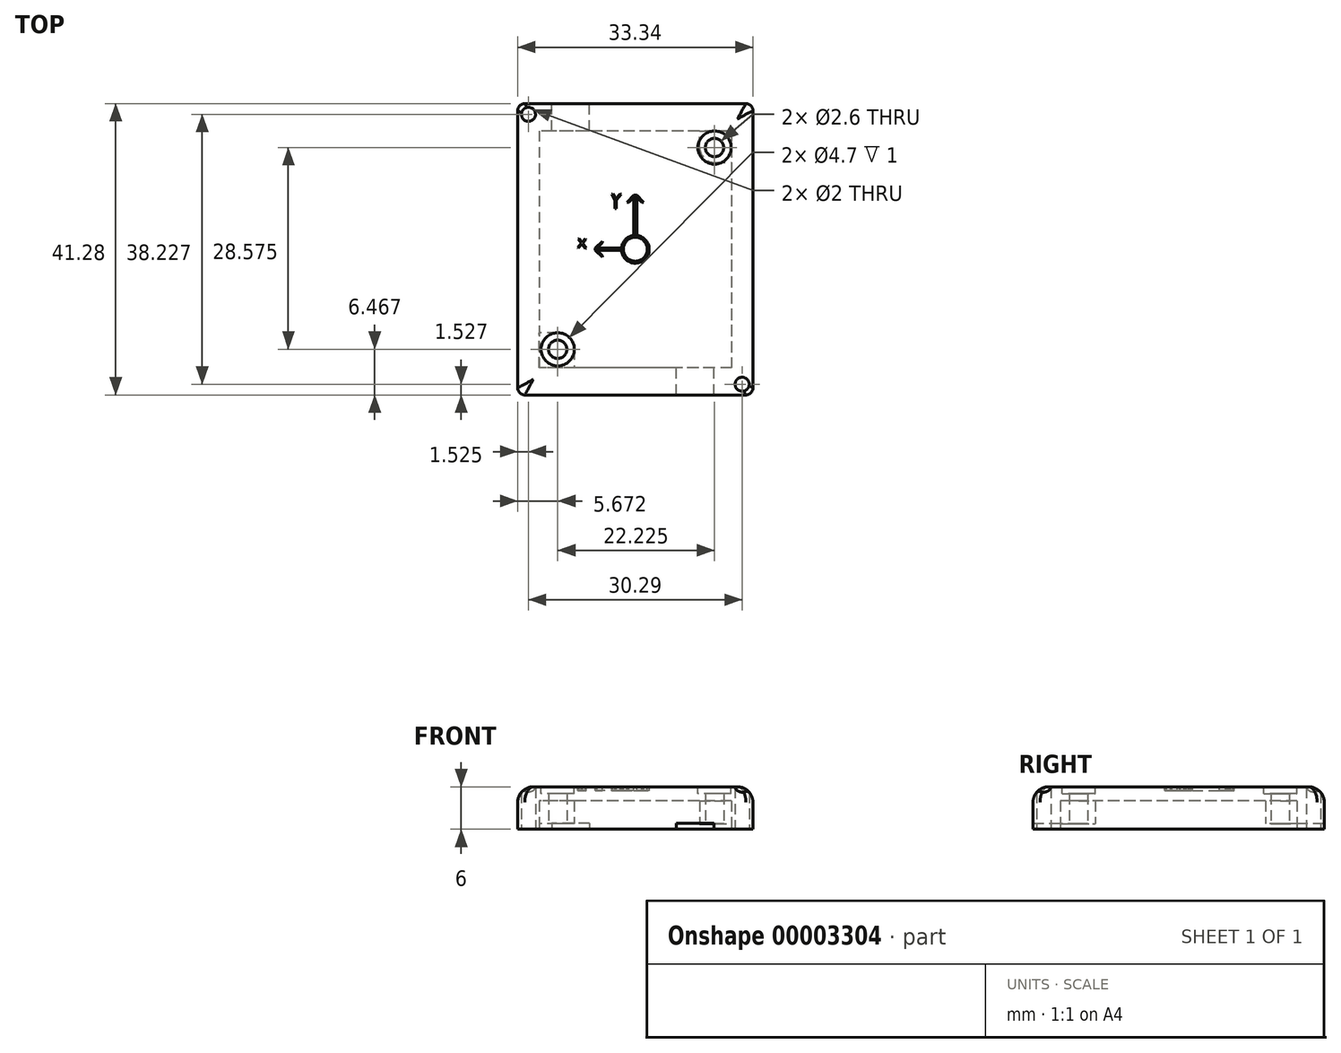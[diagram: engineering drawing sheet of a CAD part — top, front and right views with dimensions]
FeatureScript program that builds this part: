
annotation { "Feature Type Name" : "Feature", "Feature Type Description" : "" }
export const myFeature = defineFeature(function(context is Context, id is Id, definition is map)
    precondition{}
    {
        {
            var Q0;
            Q0=qCreatedBy(makeId("Top.planeOp"),FACE);
            var sketch = newSketch(context, id + "F0", { "sketchPlane" : qUnion([Q0])});
            skLineSegment(sketch, "E0.rect.bottom", {"start": v(16.67, 20.64) * mm, "end": v(-16.67, 20.64) * mm});
            skLineSegment(sketch, "E0.rect.top", {"start": v(16.67, -20.64) * mm, "end": v(-16.67, -20.64) * mm});
            skLineSegment(sketch, "E0.rect.left", {"start": v(16.67, 20.64) * mm, "end": v(16.67, -20.64) * mm});
            skLineSegment(sketch, "E0.rect.right", {"start": v(-16.67, 20.64) * mm, "end": v(-16.67, -20.64) * mm});
            skPoint(sketch, "E0.rect.middle", {"position": v(0, 0) * mm});
            skSolve(sketch);
        }
        {
            var Q0;
            Q0=qSketchRegion(id+"F0",true);
            extrude(context, id + "F1", {"entities" : qUnion([Q0]), "oppositeDirection" : true, "depth" : 6 * mm});
        }
        {
            var Q0;
            Q0=makeQuery(id+"F1.opExtrude","CAP_FACE",FACE,{"disambiguationData":[OSD([sQuery(id+"F0.wireOp",EDGE,"E0.rect.bottom"),sQuery(id+"F0.wireOp",EDGE,"E0.rect.top"),sQuery(id+"F0.wireOp",EDGE,"E0.rect.left"),sQuery(id+"F0.wireOp",EDGE,"E0.rect.right")])],"isStart":true});
            var sketch = newSketch(context, id + "F2", { "sketchPlane" : qUnion([Q0])});
            skLineSegment(sketch, "E1.rect.bottom", {"start": v(13.33, 16.51) * mm, "end": v(-13.34, 16.51) * mm});
            skLineSegment(sketch, "E1.rect.top", {"start": v(13.34, -16.51) * mm, "end": v(-13.33, -16.51) * mm});
            skLineSegment(sketch, "E1.rect.left", {"start": v(13.33, 16.51) * mm, "end": v(13.34, -16.51) * mm});
            skLineSegment(sketch, "E1.rect.right", {"start": v(-13.34, 16.51) * mm, "end": v(-13.33, -16.51) * mm});
            skPoint(sketch, "E1.rect.middle", {"position": v(0, 0) * mm});
            skCircle(sketch, "E2", {"center": v(11.23, 14.4) * mm, "radius": 1.25 * mm});
            skCircle(sketch, "E3", {"center": v(-11, -14.17) * mm, "radius": 1.25 * mm});
            skCircle(sketch, "E4", {"center": v(11.23, 14.4) * mm, "radius": 2.1 * mm});
            skCircle(sketch, "E5", {"center": v(-11, -14.17) * mm, "radius": 2.34 * mm});
            skLineSegment(sketch, "E6.0", {"start": v(13.59, 16.76) * mm, "end": v(-13.59, 16.76) * mm});
            skLineSegment(sketch, "E6.1", {"start": v(13.59, 16.76) * mm, "end": v(13.59, -16.76) * mm});
            skLineSegment(sketch, "E6.2", {"start": v(13.59, -16.76) * mm, "end": v(-13.59, -16.76) * mm});
            skLineSegment(sketch, "E6.3", {"start": v(-13.59, 16.76) * mm, "end": v(-13.59, -16.76) * mm});
            skLineSegment(sketch, "E7", {"start": v(9.12, 14.4) * mm, "end": v(9.12, 16.76) * mm});
            skLineSegment(sketch, "E8", {"start": v(11.23, 12.3) * mm, "end": v(13.59, 12.3) * mm});
            skLineSegment(sketch, "E9", {"start": v(-11, -11.84) * mm, "end": v(-13.59, -11.84) * mm});
            skLineSegment(sketch, "E10", {"start": v(-8.66, -14.17) * mm, "end": v(-8.66, -16.76) * mm});
            skSolve(sketch);
        }
        {
            var Q0;
            {var subQ6=sQuery(id+"F2.wireOp",EDGE,"E1.rect.right");var subQ10=sQuery(id+"F2.wireOp",EDGE,"E1.rect.bottom");var subQ18=makeQuery(id+"F2.imprint","INTERSECT",VERTEX,{"derivedFrom":[subQ10,subQ6]});Q0=makeQuery(id+"F2.imprint","IMPRINT",FACE,{"disambiguationData":[TD([[makeQuery(id+"F2.imprint","IMPRINT",EDGE,{"disambiguationData":[TD([[subQ18,1.0]])],"derivedFrom":subQ10}),1.0]])]});}
            var Q1;
            {var subQ1=sQuery(id+"F2.wireOp",EDGE,"E1.rect.right");var subQ6=sQuery(id+"F2.wireOp",EDGE,"E1.rect.bottom");var subQ11=makeQuery(id+"F2.imprint","INTERSECT",VERTEX,{"derivedFrom":[subQ6,subQ1]});Q1=makeQuery(id+"F2.imprint","IMPRINT",FACE,{"disambiguationData":[TD([[makeQuery(id+"F2.imprint","IMPRINT",EDGE,{"disambiguationData":[TD([[subQ11,1.0]])],"derivedFrom":subQ6}),-1.0]])]});}
            var Q2;
            {var subQ1=sQuery(id+"F2.wireOp",EDGE,"E1.rect.left");var subQ6=sQuery(id+"F2.wireOp",EDGE,"E1.rect.top");var subQ11=makeQuery(id+"F2.imprint","INTERSECT",VERTEX,{"derivedFrom":[subQ6,subQ1]});Q2=makeQuery(id+"F2.imprint","IMPRINT",FACE,{"disambiguationData":[TD([[makeQuery(id+"F2.imprint","IMPRINT",EDGE,{"disambiguationData":[TD([[subQ11,-1.0]])],"derivedFrom":subQ6}),1.0]])]});}
            extrude(context, id + "F3", {"entities" : qUnion([Q0, Q1, Q2]), "operationType" : NewBodyOperationType.REMOVE, "oppositeDirection" : true, "depth" : 4 * mm});
        }
        {
            var Q0;
            Q0=makeQuery(id+"F1.opExtrude","CAP_FACE",FACE,{"disambiguationData":[OSD([sQuery(id+"F0.wireOp",EDGE,"E0.rect.bottom"),sQuery(id+"F0.wireOp",EDGE,"E0.rect.top"),sQuery(id+"F0.wireOp",EDGE,"E0.rect.left"),sQuery(id+"F0.wireOp",EDGE,"E0.rect.right")])],"isStart":true});
            var sketch = newSketch(context, id + "F4", { "sketchPlane" : qUnion([Q0])});
            skLineSegment(sketch, "E11", {"start": v(9.12, 16.76) * mm, "end": v(13.59, 16.76) * mm});
            skLineSegment(sketch, "E12", {"start": v(13.59, 16.76) * mm, "end": v(13.59, 12.3) * mm});
            skLineSegment(sketch, "E13", {"start": v(13.59, 12.3) * mm, "end": v(11.23, 12.3) * mm});
            skArc(sketch, "E14", {"start": v(9.12, 14.4) * mm, "mid": v(9.74, 12.91) * mm, "end": v(11.23, 12.3) * mm});
            skLineSegment(sketch, "E15", {"start": v(9.12, 14.4) * mm, "end": v(9.12, 16.76) * mm});
            skArc(sketch, "E16", {"start": v(-8.66, -14.17) * mm, "mid": v(-9.35, -12.52) * mm, "end": v(-11, -11.84) * mm});
            skLineSegment(sketch, "E17", {"start": v(-8.66, -14.17) * mm, "end": v(-8.66, -16.76) * mm});
            skLineSegment(sketch, "E18", {"start": v(-8.66, -16.76) * mm, "end": v(-13.59, -16.76) * mm});
            skLineSegment(sketch, "E19", {"start": v(-13.59, -16.76) * mm, "end": v(-13.59, -11.84) * mm});
            skLineSegment(sketch, "E20", {"start": v(-13.59, -11.84) * mm, "end": v(-11, -11.84) * mm});
            skSolve(sketch);
        }
        {
            var Q0;
            Q0=qSketchRegion(id+"F4",true);
            extrude(context, id + "F5", {"entities" : qUnion([Q0]), "operationType" : NewBodyOperationType.REMOVE, "oppositeDirection" : true, "depth" : .8 * mm});
        }
        {
            var Q0;
            Q0=makeQuery(id+"F5.boolean.opBoolean","COPY",FACE,{"derivedFrom":makeQuery(id+"F5.opExtrude","CAP_FACE",FACE,{"disambiguationData":[OSD([sQuery(id+"F4.wireOp",EDGE,"E11"),sQuery(id+"F4.wireOp",EDGE,"E12"),sQuery(id+"F4.wireOp",EDGE,"E13"),sQuery(id+"F4.wireOp",EDGE,"E14"),sQuery(id+"F4.wireOp",EDGE,"E15")])],"isStart":false})});
            var sketch = newSketch(context, id + "F6", { "sketchPlane" : qUnion([Q0])});
            skCircle(sketch, "E21", {"center": v(11.23, 14.4) * mm, "radius": 1.3 * mm});
            skSolve(sketch);
        }
        {
            var Q0;
            Q0=qSketchRegion(id+"F6",true);
            extrude(context, id + "F7", {"entities" : qUnion([Q0]), "operationType" : NewBodyOperationType.REMOVE, "oppositeDirection" : true, "depth" : 25.4 * mm});
        }
        {
            var Q0;
            Q0=makeQuery(id+"F5.boolean.opBoolean","COPY",FACE,{"derivedFrom":makeQuery(id+"F5.opExtrude","CAP_FACE",FACE,{"disambiguationData":[OSD([sQuery(id+"F4.wireOp",EDGE,"E16"),sQuery(id+"F4.wireOp",EDGE,"E17"),sQuery(id+"F4.wireOp",EDGE,"E18"),sQuery(id+"F4.wireOp",EDGE,"E19"),sQuery(id+"F4.wireOp",EDGE,"E20")])],"isStart":false})});
            var sketch = newSketch(context, id + "F8", { "sketchPlane" : qUnion([Q0])});
            skCircle(sketch, "E22", {"center": v(-11, -14.17) * mm, "radius": 1.3 * mm});
            skSolve(sketch);
        }
        {
            var Q0;
            Q0=qSketchRegion(id+"F8",true);
            extrude(context, id + "F9", {"entities" : qUnion([Q0]), "operationType" : NewBodyOperationType.REMOVE, "oppositeDirection" : true, "depth" : 25.4 * mm});
        }
        {
            var Q0;
            Q0=makeQuery(id+"F1.opExtrude","CAP_FACE",FACE,{"disambiguationData":[OSD([sQuery(id+"F0.wireOp",EDGE,"E0.rect.bottom"),sQuery(id+"F0.wireOp",EDGE,"E0.rect.top"),sQuery(id+"F0.wireOp",EDGE,"E0.rect.left"),sQuery(id+"F0.wireOp",EDGE,"E0.rect.right")])],"isStart":true});
            var sketch = newSketch(context, id + "F10", { "sketchPlane" : qUnion([Q0])});
            skLineSegment(sketch, "E23.bottom", {"start": v(-13.59, 16.76) * mm, "end": v(-5.09, 16.76) * mm});
            skLineSegment(sketch, "E23.top", {"start": v(-13.59, 20.64) * mm, "end": v(-5.09, 20.64) * mm});
            skLineSegment(sketch, "E23.left", {"start": v(-13.59, 16.76) * mm, "end": v(-13.59, 20.64) * mm});
            skLineSegment(sketch, "E23.right", {"start": v(-5.09, 16.76) * mm, "end": v(-5.09, 20.64) * mm});
            skLineSegment(sketch, "E24.bottom", {"start": v(13.59, -16.76) * mm, "end": v(4.59, -16.76) * mm});
            skLineSegment(sketch, "E24.top", {"start": v(13.59, -20.64) * mm, "end": v(4.59, -20.64) * mm});
            skLineSegment(sketch, "E24.left", {"start": v(13.59, -16.76) * mm, "end": v(13.59, -20.64) * mm});
            skLineSegment(sketch, "E24.right", {"start": v(4.59, -16.76) * mm, "end": v(4.59, -20.64) * mm});
            skSolve(sketch);
        }
        {
            var Q0;
            Q0=qSketchRegion(id+"F10",true);
            extrude(context, id + "F11", {"entities" : qUnion([Q0]), "operationType" : NewBodyOperationType.REMOVE, "oppositeDirection" : true, "depth" : .4 * mm});
        }
        {
            var Q0;
            Q0=makeQuery(id+"F1.opExtrude","SWEPT_BODY",BODY,{"disambiguationData":[OSD([sQuery(id+"F0.wireOp",EDGE,"E0.rect.bottom"),sQuery(id+"F0.wireOp",EDGE,"E0.rect.top"),sQuery(id+"F0.wireOp",EDGE,"E0.rect.left"),sQuery(id+"F0.wireOp",EDGE,"E0.rect.right")])]});
            var Q1;
            Q1=qCreatedBy(makeId("Top.planeOp"),FACE);
            mirror(context, id + "F12", {"entities" : qUnion([Q0]), "mirrorPlane" : qUnion([Q1])});
        }
        {
            var Q0;
            Q0=makeQuery(id+"F1.opExtrude","SWEPT_BODY",BODY,{"disambiguationData":[OSD([sQuery(id+"F0.wireOp",EDGE,"E0.rect.bottom"),sQuery(id+"F0.wireOp",EDGE,"E0.rect.top"),sQuery(id+"F0.wireOp",EDGE,"E0.rect.left"),sQuery(id+"F0.wireOp",EDGE,"E0.rect.right")])]});
            deleteBodies(context, id + "F13", {"entities" : qUnion([Q0])});
        }
        {
            var Q0;
            Q0=makeQuery(id+"F12.opPattern","COPY",FACE,{"derivedFrom":makeQuery(id+"F1.opExtrude","CAP_FACE",FACE,{"disambiguationData":[OSD([sQuery(id+"F0.wireOp",EDGE,"E0.rect.bottom"),sQuery(id+"F0.wireOp",EDGE,"E0.rect.top"),sQuery(id+"F0.wireOp",EDGE,"E0.rect.left"),sQuery(id+"F0.wireOp",EDGE,"E0.rect.right")])],"isStart":false}),"instanceName":"1"});
            var sketch = newSketch(context, id + "F14", { "sketchPlane" : qUnion([Q0])});
            skCircle(sketch, "E25", {"center": v(11.23, 14.4) * mm, "radius": 2.35 * mm});
            skCircle(sketch, "E26", {"center": v(-11, -14.17) * mm, "radius": 2.35 * mm});
            skSolve(sketch);
        }
        {
            var Q0;
            Q0 = qSketchRegion(id + "F14", true);
            extrude(context, id + "F15", {"entities" : qUnion([Q0]), "operationType" : NewBodyOperationType.REMOVE, "oppositeDirection" : true, "depth" : 1 * mm});
        }
        {
            var Q0;
            {var subQ0=sQuery(id+"F0.wireOp",EDGE,"E0.rect.bottom");var subQ1=sQuery(id+"F0.wireOp",EDGE,"E0.rect.top");var subQ2=sQuery(id+"F0.wireOp",EDGE,"E0.rect.right");Q0=makeQuery(id+"F12.opPattern","COPY",FACE,{"derivedFrom":makeQuery(id+"F11.boolean.opBoolean","SPLIT",FACE,{"disambiguationData":[TD([makeQuery(id+"F1.opExtrude","SWEPT_FACE",FACE,{"disambiguationData":[OSD([subQ2])]})])],"derivedFrom":makeQuery(id+"F1.opExtrude","CAP_FACE",FACE,{"disambiguationData":[OSD([subQ0,subQ1,sQuery(id+"F0.wireOp",EDGE,"E0.rect.left"),subQ2])],"isStart":true})}),"instanceName":"1"});}
            var sketch = newSketch(context, id + "F16", { "sketchPlane" : qUnion([Q0])});
            skCircle(sketch, "E27", {"center": v(-15.14, -19.11) * mm, "radius": 1 * mm});
            skSolve(sketch);
        }
        {
            var Q0;
            Q0=makeQuery(id+"F16.imprint","IMPRINT",FACE,{"disambiguationData":[TD([[makeQuery(id+"F16.imprint","IMPRINT",EDGE,{"derivedFrom":sQuery(id+"F16.wireOp",EDGE,"E27")}),1.0]])]});
            extrude(context, id + "F17", {"entities" : qUnion([Q0]), "operationType" : NewBodyOperationType.REMOVE, "oppositeDirection" : true, "depth" : 20 * mm});
        }
        {
            var Q0;
            {var subQ0=sQuery(id+"F0.wireOp",EDGE,"E0.rect.bottom");var subQ1=sQuery(id+"F0.wireOp",EDGE,"E0.rect.top");var subQ2=sQuery(id+"F0.wireOp",EDGE,"E0.rect.left");Q0=makeQuery(id+"F12.opPattern","COPY",FACE,{"derivedFrom":makeQuery(id+"F11.boolean.opBoolean","SPLIT",FACE,{"disambiguationData":[TD([makeQuery(id+"F1.opExtrude","SWEPT_FACE",FACE,{"disambiguationData":[OSD([subQ2])]})])],"derivedFrom":makeQuery(id+"F1.opExtrude","CAP_FACE",FACE,{"disambiguationData":[OSD([subQ0,subQ1,subQ2,sQuery(id+"F0.wireOp",EDGE,"E0.rect.right")])],"isStart":true})}),"instanceName":"1"});}
            var sketch = newSketch(context, id + "F18", { "sketchPlane" : qUnion([Q0])});
            skCircle(sketch, "E28", {"center": v(15.14, 19.11) * mm, "radius": 1 * mm});
            skSolve(sketch);
        }
        {
            var Q0;
            Q0 = qSketchRegion(id + "F18", true);
            extrude(context, id + "F19", {"entities" : qUnion([Q0]), "operationType" : NewBodyOperationType.REMOVE, "oppositeDirection" : true, "depth" : 25 * mm});
        }
        {
            var Q0;
            Q0=makeQuery(id+"F12.opPattern","COPY",EDGE,{"derivedFrom":makeQuery(id+"F1.opExtrude","CAP_EDGE",EDGE,{"disambiguationData":[OSD([sQuery(id+"F0.wireOp",EDGE,"E0.rect.top")])],"isStart":false}),"instanceName":"1"});
            var Q1;
            Q1=makeQuery(id+"F12.opPattern","COPY",EDGE,{"derivedFrom":makeQuery(id+"F1.opExtrude","CAP_EDGE",EDGE,{"disambiguationData":[OSD([sQuery(id+"F0.wireOp",EDGE,"E0.rect.left")])],"isStart":false}),"instanceName":"1"});
            var Q2;
            Q2=makeQuery(id+"F12.opPattern","COPY",EDGE,{"derivedFrom":makeQuery(id+"F1.opExtrude","CAP_EDGE",EDGE,{"disambiguationData":[OSD([sQuery(id+"F0.wireOp",EDGE,"E0.rect.bottom")])],"isStart":false}),"instanceName":"1"});
            var Q3;
            Q3=makeQuery(id+"F12.opPattern","COPY",EDGE,{"derivedFrom":makeQuery(id+"F1.opExtrude","CAP_EDGE",EDGE,{"disambiguationData":[OSD([sQuery(id+"F0.wireOp",EDGE,"E0.rect.right")])],"isStart":false}),"instanceName":"1"});
            fillet(context, id + "F20", {"entities" : qUnion([Q0, Q1, Q2, Q3]), "radius" : 2.2 * mm, "tangentPropagation" : true, "allowEdgeOverflow" : false});
        }
        {
            var Q0;
            Q0=makeQuery(id+"F12.opPattern","COPY",EDGE,{"derivedFrom":makeQuery(id+"F1.opExtrude","SWEPT_EDGE",EDGE,{"disambiguationData":[OSD([sQuery(id+"F0.wireOp",EDGE,"E0.rect.bottom"),sQuery(id+"F0.wireOp",EDGE,"E0.rect.right")])]}),"instanceName":"1"});
            var Q1;
            Q1=makeQuery(id+"F12.opPattern","COPY",EDGE,{"derivedFrom":makeQuery(id+"F1.opExtrude","SWEPT_EDGE",EDGE,{"disambiguationData":[OSD([sQuery(id+"F0.wireOp",EDGE,"E0.rect.bottom"),sQuery(id+"F0.wireOp",EDGE,"E0.rect.left")])]}),"instanceName":"1"});
            var Q2;
            Q2=makeQuery(id+"F12.opPattern","COPY",EDGE,{"derivedFrom":makeQuery(id+"F1.opExtrude","SWEPT_EDGE",EDGE,{"disambiguationData":[OSD([sQuery(id+"F0.wireOp",EDGE,"E0.rect.top"),sQuery(id+"F0.wireOp",EDGE,"E0.rect.right")])]}),"instanceName":"1"});
            var Q3;
            Q3=makeQuery(id+"F12.opPattern","COPY",EDGE,{"derivedFrom":makeQuery(id+"F1.opExtrude","SWEPT_EDGE",EDGE,{"disambiguationData":[OSD([sQuery(id+"F0.wireOp",EDGE,"E0.rect.top"),sQuery(id+"F0.wireOp",EDGE,"E0.rect.left")])]}),"instanceName":"1"});
            fillet(context, id + "F21", {"entities" : qUnion([Q0, Q1, Q2, Q3]), "radius" : 1 * mm, "tangentPropagation" : true, "allowEdgeOverflow" : false});
        }
        {
            var Q0;
            Q0=makeQuery(id+"F12.opPattern","COPY",FACE,{"derivedFrom":makeQuery(id+"F1.opExtrude","CAP_FACE",FACE,{"disambiguationData":[OSD([sQuery(id+"F0.wireOp",EDGE,"E0.rect.bottom"),sQuery(id+"F0.wireOp",EDGE,"E0.rect.top"),sQuery(id+"F0.wireOp",EDGE,"E0.rect.left"),sQuery(id+"F0.wireOp",EDGE,"E0.rect.right")])],"isStart":false}),"instanceName":"1"});
            var sketch = newSketch(context, id + "F22", { "sketchPlane" : qUnion([Q0])});
            skCircle(sketch, "E29", {"center": v(0, 0) * mm, "radius": 1.7 * mm});
            skLineSegment(sketch, "E30", {"start": v(0, 1.7) * mm, "end": v(0, 7.65) * mm});
            skLineSegment(sketch, "E31", {"start": v(0, 7.65) * mm, "end": v(-0.93, 6.66) * mm});
            skLineSegment(sketch, "E32.0.MirrorCS", {"start": v(0, 7.65) * mm, "end": v(0.93, 6.66) * mm});
            skLineSegment(sketch, "E33", {"start": v(-1.7, 0) * mm, "end": v(-5.65, 0) * mm});
            skLineSegment(sketch, "E34", {"start": v(-5.65, 0) * mm, "end": v(-4.66, -0.93) * mm});
            skLineSegment(sketch, "E35.0.MirrorCS", {"start": v(-5.65, 0) * mm, "end": v(-4.66, 0.93) * mm});
            skLineSegment(sketch, "E36", {"start": v(0, 0) * mm, "end": v(-1.2, 1.2) * mm});
            skLineSegment(sketch, "E37", {"start": v(0, 0) * mm, "end": v(1.2, 1.2) * mm});
            skLineSegment(sketch, "E38", {"start": v(0, 0) * mm, "end": v(-1.2, -1.2) * mm});
            skLineSegment(sketch, "E39", {"start": v(0, 0) * mm, "end": v(1.2, -1.2) * mm});
            skCircle(sketch, "E40", {"center": v(0, 0) * mm, "radius": 1.97 * mm});
            skLineSegment(sketch, "E41.rect.bottom", {"start": v(-0.24, 1.69) * mm, "end": v(0.24, 1.69) * mm});
            skLineSegment(sketch, "E41.rect.top", {"start": v(-0.24, 7.67) * mm, "end": v(0.24, 7.67) * mm});
            skLineSegment(sketch, "E41.rect.left", {"start": v(-0.24, 1.69) * mm, "end": v(-0.24, 7.67) * mm});
            skLineSegment(sketch, "E41.rect.right", {"start": v(0.24, 1.69) * mm, "end": v(0.24, 7.67) * mm});
            skPoint(sketch, "E41.rect.middle", {"position": v(0, 4.68) * mm});
            skLineSegment(sketch, "E42", {"start": v(-0.24, 7.67) * mm, "end": v(-1.2, 6.66) * mm});
            skLineSegment(sketch, "E43", {"start": v(-1.2, 6.66) * mm, "end": v(-0.93, 6.66) * mm});
            skLineSegment(sketch, "E44", {"start": v(0.24, 7.67) * mm, "end": v(1.2, 6.66) * mm});
            skLineSegment(sketch, "E45", {"start": v(1.2, 6.66) * mm, "end": v(0.93, 6.66) * mm});
            skLineSegment(sketch, "E46.rect.bottom", {"start": v(-1.7, -0.18) * mm, "end": v(-5.66, -0.18) * mm});
            skLineSegment(sketch, "E46.rect.top", {"start": v(-1.7, 0.18) * mm, "end": v(-5.66, 0.18) * mm});
            skLineSegment(sketch, "E46.rect.left", {"start": v(-1.7, -0.18) * mm, "end": v(-1.7, 0.18) * mm});
            skLineSegment(sketch, "E46.rect.right", {"start": v(-5.66, -0.18) * mm, "end": v(-5.66, 0.18) * mm});
            skPoint(sketch, "E46.rect.middle", {"position": v(-3.68, 0) * mm});
            skLineSegment(sketch, "E47", {"start": v(-5.66, 0.18) * mm, "end": v(-4.66, 1.12) * mm});
            skLineSegment(sketch, "E48", {"start": v(-4.66, 1.12) * mm, "end": v(-4.66, 0.93) * mm});
            skLineSegment(sketch, "E49", {"start": v(-5.66, -0.18) * mm, "end": v(-4.66, -1.12) * mm});
            skLineSegment(sketch, "E50", {"start": v(-4.66, -1.12) * mm, "end": v(-4.66, -0.93) * mm});
            skLineSegment(sketch, "E51", {"start": v(-8.1, 1.43) * mm, "end": v(-7.1, 0.12) * mm});
            skLineSegment(sketch, "E52", {"start": v(-7.01, 1.4) * mm, "end": v(-8.09, 0.18) * mm});
            skLineSegment(sketch, "E53", {"start": v(-8.09, 0.18) * mm, "end": v(-8.18, 0.26) * mm});
            skLineSegment(sketch, "E54", {"start": v(-8.18, 0.26) * mm, "end": v(-7.1, 1.48) * mm});
            skLineSegment(sketch, "E55", {"start": v(-7.1, 1.48) * mm, "end": v(-7.01, 1.4) * mm});
            skLineSegment(sketch, "E56", {"start": v(-8.1, 1.43) * mm, "end": v(-7.98, 1.52) * mm});
            skLineSegment(sketch, "E57", {"start": v(-7.98, 1.52) * mm, "end": v(-6.97, 0.2) * mm});
            skLineSegment(sketch, "E58", {"start": v(-6.97, 0.2) * mm, "end": v(-7.1, 0.12) * mm});
            skLineSegment(sketch, "E59", {"start": v(-2.86, 6.93) * mm, "end": v(-2.86, 5.77) * mm});
            skLineSegment(sketch, "E60", {"start": v(-2.86, 5.77) * mm, "end": v(-2.7, 5.77) * mm});
            skLineSegment(sketch, "E61", {"start": v(-2.7, 5.77) * mm, "end": v(-2.7, 6.95) * mm});
            skLineSegment(sketch, "E62", {"start": v(-2.7, 6.95) * mm, "end": v(-2.03, 7.8) * mm});
            skLineSegment(sketch, "E63", {"start": v(-2.03, 7.8) * mm, "end": v(-2.14, 7.88) * mm});
            skLineSegment(sketch, "E64", {"start": v(-2.14, 7.88) * mm, "end": v(-2.74, 7.12) * mm});
            skLineSegment(sketch, "E65", {"start": v(-2.74, 7.12) * mm, "end": v(-3.19, 7.85) * mm});
            skLineSegment(sketch, "E66", {"start": v(-3.19, 7.85) * mm, "end": v(-3.32, 7.77) * mm});
            skLineSegment(sketch, "E67", {"start": v(-3.32, 7.77) * mm, "end": v(-2.86, 6.93) * mm});
            skSolve(sketch);
        }
        {
            var Q0;
            {var subQ3=sQuery(id+"F22.wireOp",EDGE,"E29");var subQ10=makeQuery(id+"F22.imprint","INTERSECT",VERTEX,{"derivedFrom":[subQ3,sQuery(id+"F22.wireOp",EDGE,"E38")]});Q0=makeQuery(id+"F22.imprint","IMPRINT",FACE,{"disambiguationData":[TD([[makeQuery(id+"F22.imprint","IMPRINT",EDGE,{"disambiguationData":[TD([[subQ10,-1.0]])],"derivedFrom":subQ3}),-1.0]])]});}
            var Q1;
            {var subQ1=sQuery(id+"F22.wireOp",EDGE,"E40");var subQ5=sQuery(id+"F22.wireOp",EDGE,"E41.rect.left");var subQ6=makeQuery(id+"F22.imprint","INTERSECT",VERTEX,{"derivedFrom":[subQ1,subQ5]});Q1=makeQuery(id+"F22.imprint","IMPRINT",FACE,{"disambiguationData":[TD([[makeQuery(id+"F22.imprint","IMPRINT",EDGE,{"disambiguationData":[TD([[subQ6,-1.0]])],"derivedFrom":subQ1}),1.0]])]});}
            var Q2;
            {var subQ3=sQuery(id+"F22.wireOp",EDGE,"E29");var subQ5=sQuery(id+"F22.wireOp",EDGE,"E30");var subQ7=makeQuery(id+"F22.imprint","INTERSECT",VERTEX,{"derivedFrom":[subQ3,subQ5]});Q2=makeQuery(id+"F22.imprint","IMPRINT",FACE,{"disambiguationData":[TD([[makeQuery(id+"F22.imprint","IMPRINT",EDGE,{"disambiguationData":[TD([[subQ7,-1.0]])],"derivedFrom":subQ5}),1.0]])]});}
            var Q3;
            {var subQ3=sQuery(id+"F22.wireOp",EDGE,"E29");var subQ5=sQuery(id+"F22.wireOp",EDGE,"E30");var subQ7=makeQuery(id+"F22.imprint","INTERSECT",VERTEX,{"derivedFrom":[subQ3,subQ5]});Q3=makeQuery(id+"F22.imprint","IMPRINT",FACE,{"disambiguationData":[TD([[makeQuery(id+"F22.imprint","IMPRINT",EDGE,{"disambiguationData":[TD([[subQ7,-1.0]])],"derivedFrom":subQ5}),-1.0]])]});}
            var Q4;
            {var subQ1=sQuery(id+"F22.wireOp",EDGE,"E40");var subQ5=sQuery(id+"F22.wireOp",EDGE,"E30");var subQ6=makeQuery(id+"F22.imprint","INTERSECT",VERTEX,{"derivedFrom":[subQ5,subQ1]});Q4=makeQuery(id+"F22.imprint","IMPRINT",FACE,{"disambiguationData":[TD([[makeQuery(id+"F22.imprint","IMPRINT",EDGE,{"disambiguationData":[TD([[subQ6,-1.0]])],"derivedFrom":subQ1}),-1.0]])]});}
            var Q5;
            {var subQ1=sQuery(id+"F22.wireOp",EDGE,"E40");var subQ5=sQuery(id+"F22.wireOp",EDGE,"E30");var subQ6=makeQuery(id+"F22.imprint","INTERSECT",VERTEX,{"derivedFrom":[subQ5,subQ1]});Q5=makeQuery(id+"F22.imprint","IMPRINT",FACE,{"disambiguationData":[TD([[makeQuery(id+"F22.imprint","IMPRINT",EDGE,{"disambiguationData":[TD([[subQ6,1.0]])],"derivedFrom":subQ1}),-1.0]])]});}
            var Q6;
            {var subQ1=sQuery(id+"F22.wireOp",EDGE,"E40");var subQ5=sQuery(id+"F22.wireOp",EDGE,"E33");var subQ6=makeQuery(id+"F22.imprint","INTERSECT",VERTEX,{"derivedFrom":[subQ5,subQ1]});Q6=makeQuery(id+"F22.imprint","IMPRINT",FACE,{"disambiguationData":[TD([[makeQuery(id+"F22.imprint","IMPRINT",EDGE,{"disambiguationData":[TD([[subQ6,1.0]])],"derivedFrom":subQ1}),-1.0]])]});}
            var Q7;
            {var subQ1=sQuery(id+"F22.wireOp",EDGE,"E40");var subQ5=sQuery(id+"F22.wireOp",EDGE,"E33");var subQ6=makeQuery(id+"F22.imprint","INTERSECT",VERTEX,{"derivedFrom":[subQ5,subQ1]});Q7=makeQuery(id+"F22.imprint","IMPRINT",FACE,{"disambiguationData":[TD([[makeQuery(id+"F22.imprint","IMPRINT",EDGE,{"disambiguationData":[TD([[subQ6,-1.0]])],"derivedFrom":subQ1}),-1.0]])]});}
            var Q8;
            {var subQ3=sQuery(id+"F22.wireOp",EDGE,"E29");var subQ5=sQuery(id+"F22.wireOp",EDGE,"E33");var subQ7=makeQuery(id+"F22.imprint","INTERSECT",VERTEX,{"derivedFrom":[subQ3,subQ5]});Q8=makeQuery(id+"F22.imprint","IMPRINT",FACE,{"disambiguationData":[TD([[makeQuery(id+"F22.imprint","IMPRINT",EDGE,{"disambiguationData":[TD([[subQ7,-1.0]])],"derivedFrom":subQ5}),1.0]])]});}
            var Q9;
            {var subQ3=sQuery(id+"F22.wireOp",EDGE,"E29");var subQ5=sQuery(id+"F22.wireOp",EDGE,"E33");var subQ7=makeQuery(id+"F22.imprint","INTERSECT",VERTEX,{"derivedFrom":[subQ3,subQ5]});Q9=makeQuery(id+"F22.imprint","IMPRINT",FACE,{"disambiguationData":[TD([[makeQuery(id+"F22.imprint","IMPRINT",EDGE,{"disambiguationData":[TD([[subQ7,-1.0]])],"derivedFrom":subQ5}),-1.0]])]});}
            var Q10;
            {var subQ1=sQuery(id+"F22.wireOp",EDGE,"E49");Q10=makeQuery(id+"F22.imprint","IMPRINT",FACE,{"disambiguationData":[TD([[makeQuery(id+"F22.imprint","IMPRINT",EDGE,{"derivedFrom":subQ1}),1.0]])]});}
            var Q11;
            {var subQ1=sQuery(id+"F22.wireOp",EDGE,"E47");Q11=makeQuery(id+"F22.imprint","IMPRINT",FACE,{"disambiguationData":[TD([[makeQuery(id+"F22.imprint","IMPRINT",EDGE,{"derivedFrom":subQ1}),-1.0]])]});}
            var Q12;
            {var subQ0=sQuery(id+"F22.wireOp",EDGE,"E46.rect.right");Q12=makeQuery(id+"F22.imprint","IMPRINT",FACE,{"disambiguationData":[TD([[makeQuery(id+"F22.imprint","IMPRINT",EDGE,{"derivedFrom":subQ0}),-1.0]])]});}
            var Q13;
            {var subQ1=sQuery(id+"F22.wireOp",EDGE,"E42");Q13=makeQuery(id+"F22.imprint","IMPRINT",FACE,{"disambiguationData":[TD([[makeQuery(id+"F22.imprint","IMPRINT",EDGE,{"derivedFrom":subQ1}),1.0]])]});}
            var Q14;
            {var subQ3=sQuery(id+"F22.wireOp",EDGE,"E41.rect.top");Q14=makeQuery(id+"F22.imprint","IMPRINT",FACE,{"disambiguationData":[TD([[makeQuery(id+"F22.imprint","IMPRINT",EDGE,{"derivedFrom":subQ3}),-1.0]])]});}
            var Q15;
            {var subQ1=sQuery(id+"F22.wireOp",EDGE,"E44");Q15=makeQuery(id+"F22.imprint","IMPRINT",FACE,{"disambiguationData":[TD([[makeQuery(id+"F22.imprint","IMPRINT",EDGE,{"derivedFrom":subQ1}),-1.0]])]});}
            var Q16;
            Q16=makeQuery(id+"F22.imprint","IMPRINT",FACE,{"disambiguationData":[TD([[makeQuery(id+"F22.imprint","IMPRINT",EDGE,{"derivedFrom":sQuery(id+"F22.wireOp",EDGE,"E59")}),1.0]])]});
            var Q17;
            {var subQ5=sQuery(id+"F22.wireOp",EDGE,"E55");Q17=makeQuery(id+"F22.imprint","IMPRINT",FACE,{"disambiguationData":[TD([[makeQuery(id+"F22.imprint","IMPRINT",EDGE,{"derivedFrom":subQ5}),-1.0]])]});}
            var Q18;
            {var subQ1=sQuery(id+"F22.wireOp",EDGE,"E54");var subQ5=sQuery(id+"F22.wireOp",EDGE,"E51");var subQ6=makeQuery(id+"F22.imprint","INTERSECT",VERTEX,{"derivedFrom":[subQ5,subQ1]});Q18=makeQuery(id+"F22.imprint","IMPRINT",FACE,{"disambiguationData":[TD([[makeQuery(id+"F22.imprint","IMPRINT",EDGE,{"disambiguationData":[TD([[subQ6,-1.0]])],"derivedFrom":subQ5}),1.0]])]});}
            var Q19;
            {var subQ3=sQuery(id+"F22.wireOp",EDGE,"E53");Q19=makeQuery(id+"F22.imprint","IMPRINT",FACE,{"disambiguationData":[TD([[makeQuery(id+"F22.imprint","IMPRINT",EDGE,{"derivedFrom":subQ3}),-1.0]])]});}
            var Q20;
            {var subQ0=sQuery(id+"F22.wireOp",EDGE,"E58");Q20=makeQuery(id+"F22.imprint","IMPRINT",FACE,{"disambiguationData":[TD([[makeQuery(id+"F22.imprint","IMPRINT",EDGE,{"derivedFrom":subQ0}),-1.0]])]});}
            var Q21;
            {var subQ3=sQuery(id+"F22.wireOp",EDGE,"E56");Q21=makeQuery(id+"F22.imprint","IMPRINT",FACE,{"disambiguationData":[TD([[makeQuery(id+"F22.imprint","IMPRINT",EDGE,{"derivedFrom":subQ3}),-1.0]])]});}
            extrude(context, id + "F23", {"entities" : qUnion([Q0, Q1, Q2, Q3, Q4, Q5, Q6, Q7, Q8, Q9, Q10, Q11, Q12, Q13, Q14, Q15, Q16, Q17, Q18, Q19, Q20, Q21]), "operationType" : NewBodyOperationType.REMOVE, "oppositeDirection" : true, "depth" : 0.5 * mm});
        }
        {
            var Q0;
            Q0=makeQuery(id+"F12.opPattern","COPY",FACE,{"derivedFrom":makeQuery(id+"F11.boolean.opBoolean","COPY",FACE,{"derivedFrom":makeQuery(id+"F11.opExtrude","CAP_FACE",FACE,{"disambiguationData":[OSD([sQuery(id+"F10.wireOp",EDGE,"E24.bottom"),sQuery(id+"F10.wireOp",EDGE,"E24.top"),sQuery(id+"F10.wireOp",EDGE,"E24.left"),sQuery(id+"F10.wireOp",EDGE,"E24.right")])],"isStart":false})}),"instanceName":"1"});
            var sketch = newSketch(context, id + "F24", { "sketchPlane" : qUnion([Q0])});
            skLineSegment(sketch, "E68.bottom", {"start": v(4.59, 20.64) * mm, "end": v(13.59, 20.64) * mm});
            skLineSegment(sketch, "E68.top", {"start": v(4.59, 16.76) * mm, "end": v(13.59, 16.76) * mm});
            skLineSegment(sketch, "E68.left", {"start": v(4.59, 20.64) * mm, "end": v(4.59, 16.76) * mm});
            skLineSegment(sketch, "E68.right", {"start": v(13.59, 20.64) * mm, "end": v(13.59, 16.76) * mm});
            skSolve(sketch);
        }
        {
            var Q0;
            Q0 = qSketchRegion(id + "F24", true);
            extrude(context, id + "F25", {"entities" : qUnion([Q0]), "operationType" : NewBodyOperationType.ADD, "depth" : .4 * mm});
        }
        {
            var Q0;
            Q0=makeQuery(id+"F12.opPattern","COPY",FACE,{"derivedFrom":makeQuery(id+"F11.boolean.opBoolean","COPY",FACE,{"derivedFrom":makeQuery(id+"F11.opExtrude","CAP_FACE",FACE,{"disambiguationData":[OSD([sQuery(id+"F10.wireOp",EDGE,"E23.bottom"),sQuery(id+"F10.wireOp",EDGE,"E23.top"),sQuery(id+"F10.wireOp",EDGE,"E23.left"),sQuery(id+"F10.wireOp",EDGE,"E23.right")])],"isStart":false})}),"instanceName":"1"});
            var sketch = newSketch(context, id + "F26", { "sketchPlane" : qUnion([Q0])});
            skLineSegment(sketch, "E69.bottom", {"start": v(-5.09, -20.64) * mm, "end": v(-13.59, -20.64) * mm});
            skLineSegment(sketch, "E69.top", {"start": v(-5.09, -16.76) * mm, "end": v(-13.59, -16.76) * mm});
            skLineSegment(sketch, "E69.left", {"start": v(-5.09, -20.64) * mm, "end": v(-5.09, -16.76) * mm});
            skLineSegment(sketch, "E69.right", {"start": v(-13.59, -20.64) * mm, "end": v(-13.59, -16.76) * mm});
            skSolve(sketch);
        }
        {
            var Q0;
            Q0 = qSketchRegion(id + "F26", true);
            extrude(context, id + "F27", {"entities" : qUnion([Q0]), "operationType" : NewBodyOperationType.ADD, "depth" : .4 * mm});
        }
        {
            var Q0;
            {var subQ0=sQuery(id+"F0.wireOp",EDGE,"E0.rect.bottom");var subQ1=sQuery(id+"F0.wireOp",EDGE,"E0.rect.top");var subQ2=sQuery(id+"F0.wireOp",EDGE,"E0.rect.left");var subQ3=sQuery(id+"F0.wireOp",EDGE,"E0.rect.right");var subQ4=makeQuery(id+"F1.opExtrude","CAP_FACE",FACE,{"disambiguationData":[OSD([subQ0,subQ1,subQ2,subQ3])],"isStart":true});Q0=makeQuery(id+"F27.boolean.opBoolean","MERGE",FACE,{"derivedFrom":[makeQuery(id+"F25.boolean.opBoolean","MERGE",FACE,{"derivedFrom":[makeQuery(id+"F12.opPattern","COPY",FACE,{"derivedFrom":makeQuery(id+"F11.boolean.opBoolean","SPLIT",FACE,{"disambiguationData":[TD([makeQuery(id+"F1.opExtrude","SWEPT_FACE",FACE,{"disambiguationData":[OSD([subQ3])]})])],"derivedFrom":subQ4}),"instanceName":"1"}),makeQuery(id+"F12.opPattern","COPY",FACE,{"derivedFrom":makeQuery(id+"F11.boolean.opBoolean","SPLIT",FACE,{"disambiguationData":[TD([makeQuery(id+"F1.opExtrude","SWEPT_FACE",FACE,{"disambiguationData":[OSD([subQ2])]})])],"derivedFrom":subQ4}),"instanceName":"1"}),makeQuery(id+"F25.opExtrude","CAP_FACE",FACE,{"disambiguationData":[OSD([sQuery(id+"F24.wireOp",EDGE,"E68.bottom"),sQuery(id+"F24.wireOp",EDGE,"E68.top"),sQuery(id+"F24.wireOp",EDGE,"E68.left"),sQuery(id+"F24.wireOp",EDGE,"E68.right")])],"isStart":false})]}),makeQuery(id+"F27.opExtrude","CAP_FACE",FACE,{"disambiguationData":[OSD([sQuery(id+"F26.wireOp",EDGE,"E69.bottom"),sQuery(id+"F26.wireOp",EDGE,"E69.top"),sQuery(id+"F26.wireOp",EDGE,"E69.left"),sQuery(id+"F26.wireOp",EDGE,"E69.right")])],"isStart":false})]});}
            var sketch = newSketch(context, id + "F28", { "sketchPlane" : qUnion([Q0])});
            skLineSegment(sketch, "E70.bottom", {"start": v(5.82, 20.64) * mm, "end": v(11.12, 20.64) * mm});
            skLineSegment(sketch, "E70.top", {"start": v(5.82, 16.76) * mm, "end": v(11.12, 16.76) * mm});
            skLineSegment(sketch, "E70.left", {"start": v(5.82, 20.64) * mm, "end": v(5.82, 16.76) * mm});
            skLineSegment(sketch, "E70.right", {"start": v(11.12, 20.64) * mm, "end": v(11.12, 16.76) * mm});
            skLineSegment(sketch, "E71.bottom", {"start": v(-6.52, -16.76) * mm, "end": v(-11.82, -16.76) * mm});
            skLineSegment(sketch, "E71.top", {"start": v(-6.52, -20.64) * mm, "end": v(-11.82, -20.64) * mm});
            skLineSegment(sketch, "E71.left", {"start": v(-6.52, -16.76) * mm, "end": v(-6.52, -20.64) * mm});
            skLineSegment(sketch, "E71.right", {"start": v(-11.82, -16.76) * mm, "end": v(-11.82, -20.64) * mm});
            skSolve(sketch);
        }
        {
            var Q0;
            Q0 = qSketchRegion(id + "F28", true);
            extrude(context, id + "F29", {"entities" : qUnion([Q0]), "operationType" : NewBodyOperationType.REMOVE, "oppositeDirection" : true, "depth" : 0.85 * mm});
        }
    });
